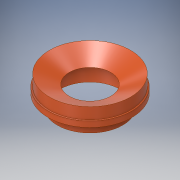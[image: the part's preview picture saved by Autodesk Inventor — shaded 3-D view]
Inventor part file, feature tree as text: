
AUTODESK INVENTOR PART (.ipt)
format: ipt  version: 2017 (Build 210142000, 142)  size: 165,888 bytes
history: native  units: in
note: dims shown in document units (in); Inventor stores cm internally (conversion verified against a paired STEP export)
features: revolve x1, sketch x1
ambient origin geometry x8: Origin, YZ Plane, XZ Plane, XY Plane, X Axis, Y Axis, Z Axis, Center Point
bodies: Solid1 (feature_tree)
feature tree (2):
  revolve  "Revolution1"  [1 undecoded]
  sketch  "Sketch1"  dims[d0=1.13in d1=3.7in d2=0.125in d3=0.1718in d5=1.0in d6=1.0in d7=90.0deg d8=0.5in d9=15.0deg d12=1.25in d13=0.25in d16=0.5in d17=0.5in d18=0.5in d19=2.5in d20=0.5in d22=0.375in d23=0.25in d25=0.234in d26=15.0deg d27=0.125in d28=0.25in d29=1.0in d30=4.25in d31=0.25in d32=1.0in d33=90.0deg]
note: 1 required parameter value undecoded (feature->parameter linkage not recoverable at this tier; creation-order binding heuristic only, values carry confidence <= 0.55)
